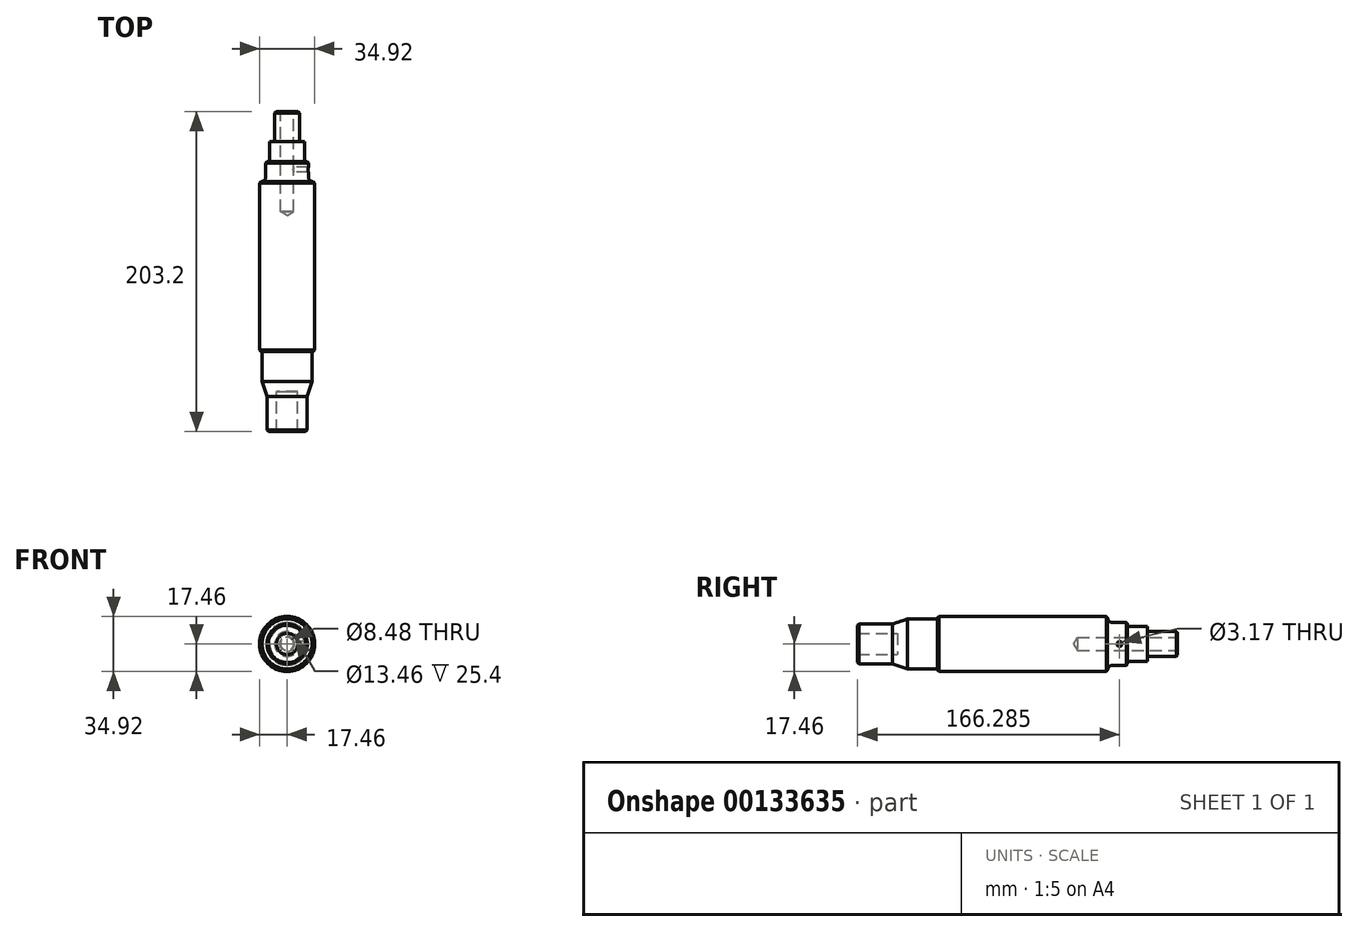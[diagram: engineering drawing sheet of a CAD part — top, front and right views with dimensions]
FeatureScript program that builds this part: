
annotation { "Feature Type Name" : "Feature", "Feature Type Description" : "" }
export const myFeature = defineFeature(function(context is Context, id is Id, definition is map)
    precondition{}
    {
        {
            var Q0;
            Q0=qCreatedBy(makeId("Right.planeOp"),FACE);
            var sketch = newSketch(context, id + "F0", { "sketchPlane" : qUnion([Q0])});
            skLineSegment(sketch, "E0", {"start": v(0, 0) * mm, "end": v(-177.8, 0) * mm});
            skLineSegment(sketch, "E1.0", {"start": v(-44.45, 17.46) * mm, "end": v(-152.4, 17.46) * mm});
            skLineSegment(sketch, "E2", {"start": v(0, 0) * mm, "end": v(0, 7.94) * mm});
            skLineSegment(sketch, "E3", {"start": v(0, 7.94) * mm, "end": v(-19.05, 7.94) * mm});
            skLineSegment(sketch, "E4", {"start": v(-19.05, 7.94) * mm, "end": v(-19.05, 11.11) * mm});
            skLineSegment(sketch, "E5", {"start": v(-31.75, 13.51) * mm, "end": v(-44.45, 13.51) * mm});
            skLineSegment(sketch, "E6", {"start": v(-44.45, 13.51) * mm, "end": v(-44.45, 17.46) * mm});
            skLineSegment(sketch, "E7", {"start": v(-177.8, 0) * mm, "end": v(-177.8, 6.73) * mm});
            skLineSegment(sketch, "E8", {"start": v(-177.8, 6.73) * mm, "end": v(-203.2, 6.73) * mm});
            skLineSegment(sketch, "E9", {"start": v(-203.2, 6.73) * mm, "end": v(-203.2, 12.7) * mm});
            skLineSegment(sketch, "E10", {"start": v(-203.2, 12.7) * mm, "end": v(-180.98, 12.7) * mm});
            skLineSegment(sketch, "E11", {"start": v(-180.98, 12.7) * mm, "end": v(-171.45, 15.87) * mm});
            skLineSegment(sketch, "E12", {"start": v(-171.45, 15.87) * mm, "end": v(-152.4, 15.87) * mm});
            skLineSegment(sketch, "E13", {"start": v(-152.4, 15.87) * mm, "end": v(-152.4, 17.46) * mm});
            skPoint(sketch, "E14.orphan", {"position": v(-152.4, 0) * mm});
            skLineSegment(sketch, "E15", {"start": v(-19.05, 11.11) * mm, "end": v(-31.75, 11.11) * mm});
            skLineSegment(sketch, "E16", {"start": v(-31.75, 11.11) * mm, "end": v(-31.75, 13.51) * mm});
            skSolve(sketch);
        }
        {
            var Q0;
            Q0=makeQuery(id+"F0.imprint","IMPRINT",FACE,{"disambiguationData":[TD([[makeQuery(id+"F0.imprint","IMPRINT",EDGE,{"derivedFrom":sQuery(id+"F0.wireOp",EDGE,"E0")}),-1.0]])]});
            var Q1;
            Q1=sQuery(id+"F0.wireOp",EDGE,"E0");
            revolve(context, id + "F1", {"entities" : qUnion([Q0]), "axis" : qUnion([Q1]), "revolveType" : RevolveType.FULL});
        }
        {
            var Q0;
            Q0=makeQuery(id+"F1.opRevolve","SWEPT_EDGE",EDGE,{"disambiguationData":[OSD([sQuery(id+"F0.wireOp",EDGE,"E9"),sQuery(id+"F0.wireOp",EDGE,"E10")])]});
            var Q1;
            Q1=makeQuery(id+"F1.opRevolve","SWEPT_EDGE",EDGE,{"disambiguationData":[OSD([sQuery(id+"F0.wireOp",EDGE,"E1.0"),sQuery(id+"F0.wireOp",EDGE,"E13")])]});
            var Q2;
            Q2=makeQuery(id+"F1.opRevolve","SWEPT_EDGE",EDGE,{"disambiguationData":[OSD([sQuery(id+"F0.wireOp",EDGE,"E1.0"),sQuery(id+"F0.wireOp",EDGE,"E6")])]});
            var Q3;
            Q3=makeQuery(id+"F1.opRevolve","SWEPT_EDGE",EDGE,{"disambiguationData":[OSD([sQuery(id+"F0.wireOp",EDGE,"E5"),sQuery(id+"F0.wireOp",EDGE,"E16")])]});
            var Q4;
            Q4=makeQuery(id+"F1.opRevolve","SWEPT_EDGE",EDGE,{"disambiguationData":[OSD([sQuery(id+"F0.wireOp",EDGE,"E2"),sQuery(id+"F0.wireOp",EDGE,"E3")])]});
            chamfer(context, id + "F2", {"entities" : qUnion([Q0, Q1, Q2, Q3, Q4]), "width" : 0.81 * mm, "tangentPropagation" : true});
        }
        {
            var Q0;
            Q0=makeQuery(id+"F1.opRevolve","SWEPT_EDGE",EDGE,{"disambiguationData":[OSD([sQuery(id+"F0.wireOp",EDGE,"E5"),sQuery(id+"F0.wireOp",EDGE,"E6")])]});
            fillet(context, id + "F3", {"entities" : qUnion([Q0]), "radius" : 3.17 * mm, "tangentPropagation" : true, "allowEdgeOverflow" : false});
        }
        {
            var Q0;
            Q0=makeQuery(id+"F1.opRevolve","SWEPT_FACE",FACE,{"disambiguationData":[OSD([sQuery(id+"F0.wireOp",EDGE,"E2")])]});
            var sketch = newSketch(context, id + "F4", { "sketchPlane" : qUnion([Q0])});
            skCircle(sketch, "E17", {"center": v(0, 0) * mm, "radius": 1.57 * mm});
            skSolve(sketch);
        }
        {
            var Q0;
            Q0=sQuery(id+"F4.wireOp",VERTEX,"E17.center");
            var Q1;
            Q1=makeQuery(id+"F1.opRevolve","SWEPT_BODY",BODY,{"disambiguationData":[OSD([sQuery(id+"F0.wireOp",EDGE,"E0"),sQuery(id+"F0.wireOp",EDGE,"E1.0"),sQuery(id+"F0.wireOp",EDGE,"E2"),sQuery(id+"F0.wireOp",EDGE,"E3"),sQuery(id+"F0.wireOp",EDGE,"E4"),sQuery(id+"F0.wireOp",EDGE,"E5"),sQuery(id+"F0.wireOp",EDGE,"E6"),sQuery(id+"F0.wireOp",EDGE,"E7"),sQuery(id+"F0.wireOp",EDGE,"E8"),sQuery(id+"F0.wireOp",EDGE,"E9"),sQuery(id+"F0.wireOp",EDGE,"E10"),sQuery(id+"F0.wireOp",EDGE,"E11"),sQuery(id+"F0.wireOp",EDGE,"E12"),sQuery(id+"F0.wireOp",EDGE,"E13"),sQuery(id+"F0.wireOp",EDGE,"E15"),sQuery(id+"F0.wireOp",EDGE,"E16")])]});
            hole(context, id + "F5", {"style" : HoleStyle.C_SINK, "endStyle" : HoleEndStyle.BLIND, "holeDiameter" : 8.48 * mm, "cSinkDiameter" : 9.52 * mm, "cSinkAngle" : 60 * degree, "holeDepth" : 63.5 * mm, "startFromSketch" : true, "locations" : qUnion([Q0]), "scope" : qUnion([Q1])});
        }
        {
            var Q0;
            Q0=qCreatedBy(makeId("Right.planeOp"),FACE);
            var sketch = newSketch(context, id + "F6", { "sketchPlane" : qUnion([Q0])});
            skCircle(sketch, "E18", {"center": v(-36.92, 0) * mm, "radius": 2 * mm});
            skSolve(sketch);
        }
        {
            var Q0;
            Q0=sQuery(id+"F6.wireOp",VERTEX,"E18.center");
            var Q1;
            Q1=makeQuery(id+"F1.opRevolve","SWEPT_BODY",BODY,{"disambiguationData":[OSD([sQuery(id+"F0.wireOp",EDGE,"E0"),sQuery(id+"F0.wireOp",EDGE,"E1.0"),sQuery(id+"F0.wireOp",EDGE,"E2"),sQuery(id+"F0.wireOp",EDGE,"E3"),sQuery(id+"F0.wireOp",EDGE,"E4"),sQuery(id+"F0.wireOp",EDGE,"E5"),sQuery(id+"F0.wireOp",EDGE,"E6"),sQuery(id+"F0.wireOp",EDGE,"E7"),sQuery(id+"F0.wireOp",EDGE,"E8"),sQuery(id+"F0.wireOp",EDGE,"E9"),sQuery(id+"F0.wireOp",EDGE,"E10"),sQuery(id+"F0.wireOp",EDGE,"E11"),sQuery(id+"F0.wireOp",EDGE,"E12"),sQuery(id+"F0.wireOp",EDGE,"E13"),sQuery(id+"F0.wireOp",EDGE,"E15"),sQuery(id+"F0.wireOp",EDGE,"E16")])]});
            hole(context, id + "F7", {"style" : HoleStyle.SIMPLE, "endStyle" : HoleEndStyle.BLIND, "oppositeDirection" : true, "holeDiameter" : 3.17 * mm, "holeDepth" : 38.1 * mm, "startFromSketch" : true, "locations" : qUnion([Q0]), "scope" : qUnion([Q1])});
        }
    });
